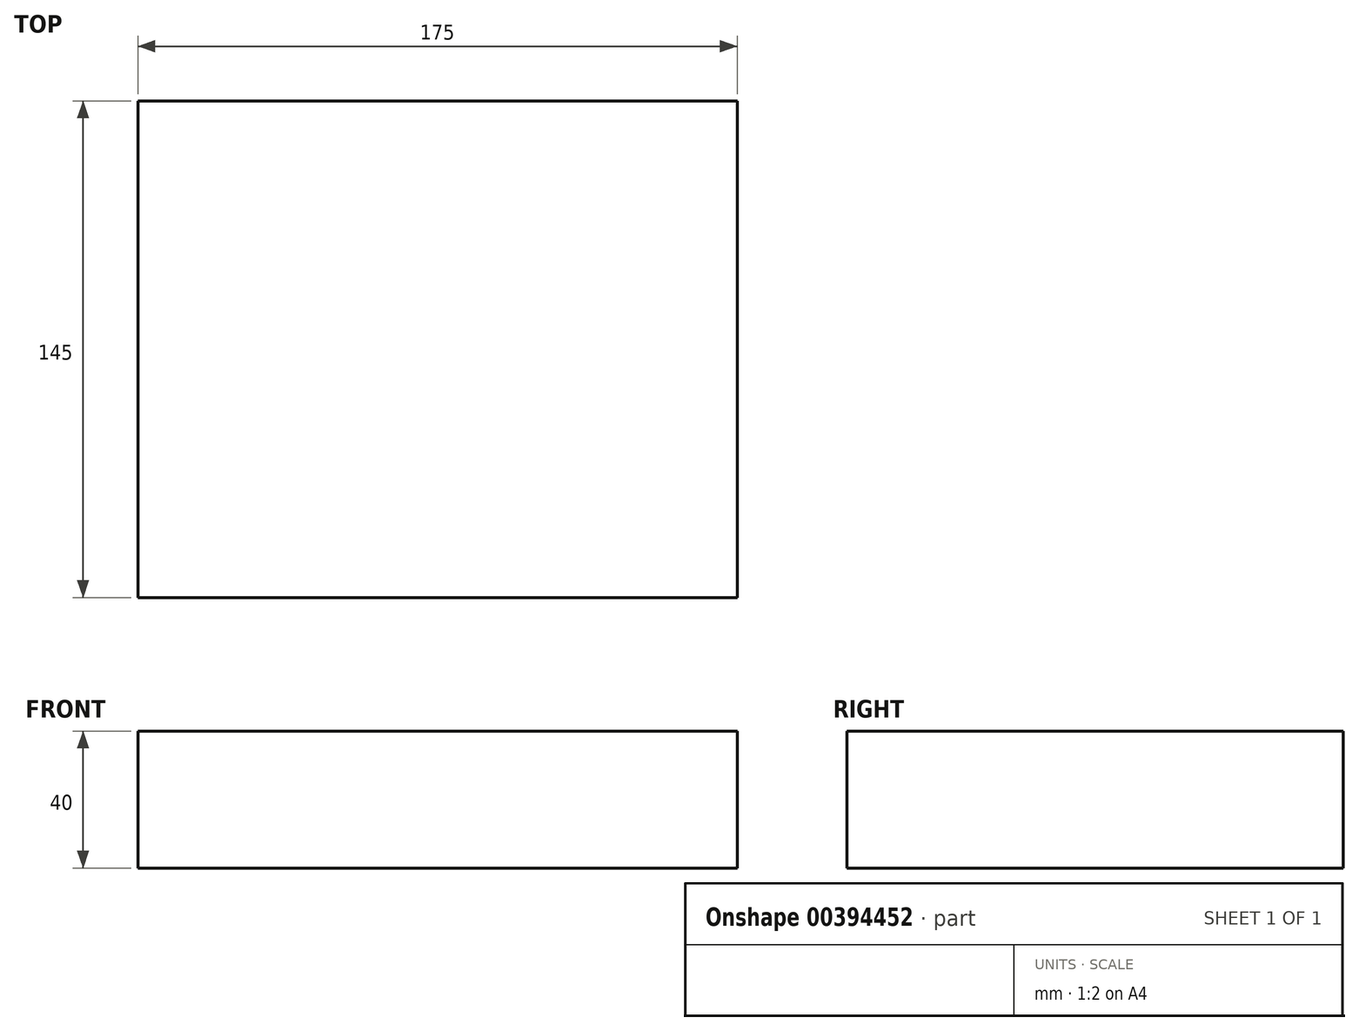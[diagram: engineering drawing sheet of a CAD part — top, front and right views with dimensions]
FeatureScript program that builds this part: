
annotation { "Feature Type Name" : "Feature", "Feature Type Description" : "" }
export const myFeature = defineFeature(function(context is Context, id is Id, definition is map)
    precondition{}
    {
        {
            var Q0;
            Q0=qCreatedBy(makeId("Top.planeOp"),FACE);
            var sketch = newSketch(context, id + "F0", { "sketchPlane" : qUnion([Q0])});
            skLineSegment(sketch, "E0.bottom", {"start": v(87.5, -72.5) * mm, "end": v(-87.5, -72.5) * mm});
            skLineSegment(sketch, "E0.top", {"start": v(87.5, 72.5) * mm, "end": v(-87.5, 72.5) * mm});
            skLineSegment(sketch, "E0.left", {"start": v(87.5, -72.5) * mm, "end": v(87.5, 72.5) * mm});
            skLineSegment(sketch, "E0.right", {"start": v(-87.5, -72.5) * mm, "end": v(-87.5, 72.5) * mm});
            skPoint(sketch, "E0.middle", {"position": v(0, 0) * mm});
            skSolve(sketch);
        }
        {
            var Q0;
            Q0 = qSketchRegion(id + "F0", true);
            extrude(context, id + "F1", {"entities" : qUnion([Q0]), "depth" : 40 * mm});
        }
    });
